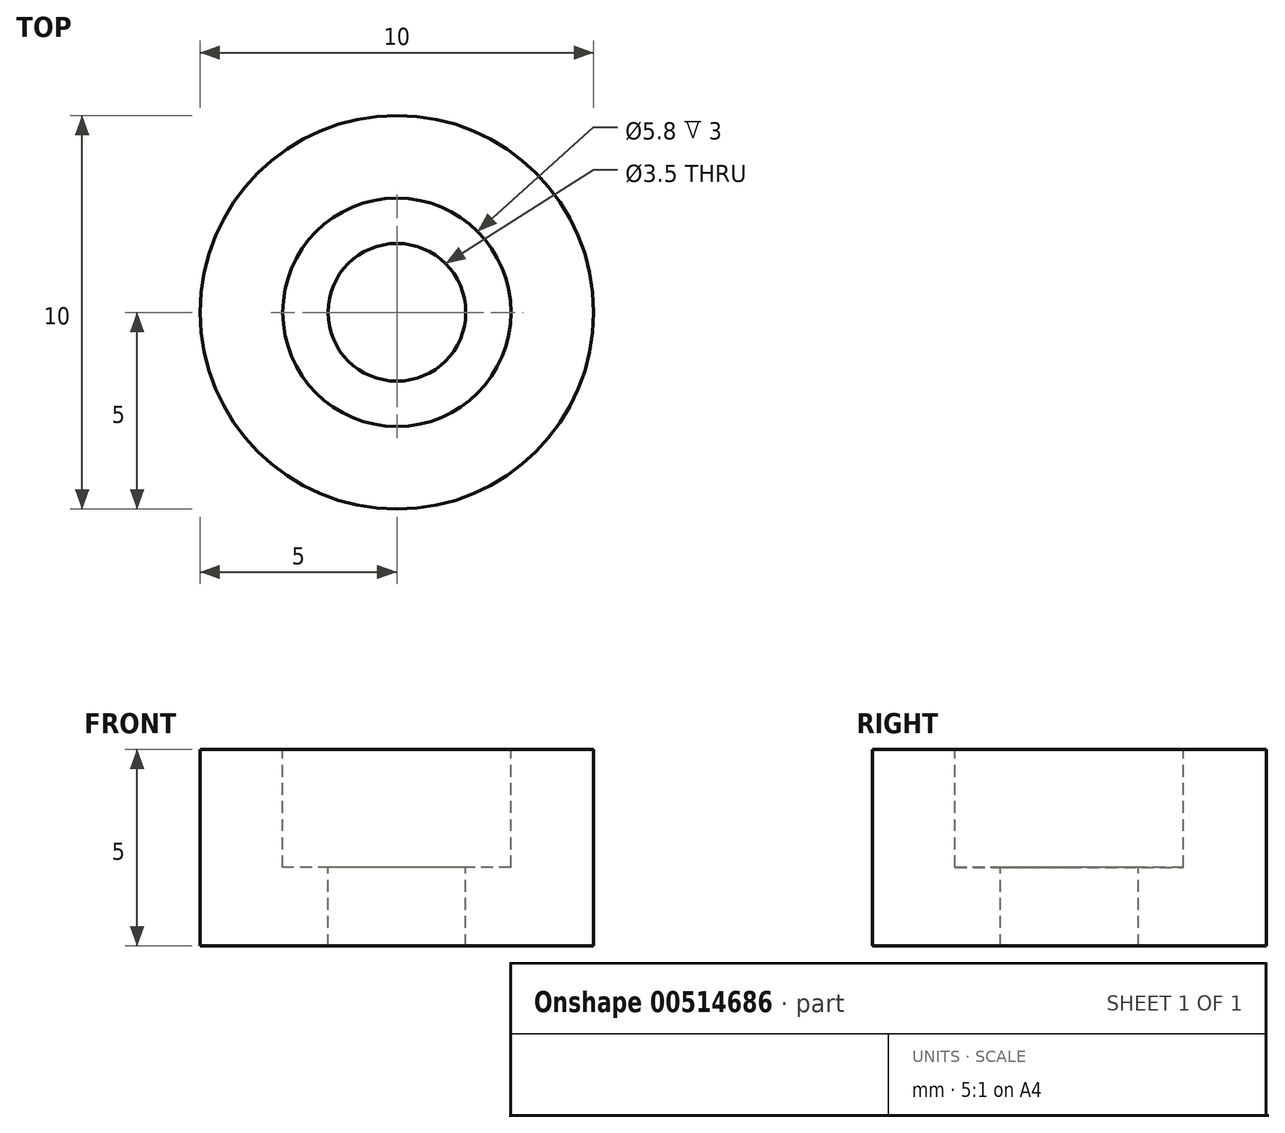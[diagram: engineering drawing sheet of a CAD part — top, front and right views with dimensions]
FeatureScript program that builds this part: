
annotation { "Feature Type Name" : "Feature", "Feature Type Description" : "" }
export const myFeature = defineFeature(function(context is Context, id is Id, definition is map)
    precondition{}
    {
        {
            var Q0;
            Q0=qCreatedBy(makeId("Top.planeOp"),FACE);
            var sketch = newSketch(context, id + "F0", { "sketchPlane" : qUnion([Q0])});
            skCircle(sketch, "E0", {"center": v(0, 0) * mm, "radius": 5 * mm});
            skSolve(sketch);
        }
        {
            var Q0;
            Q0=makeQuery(id+"F0.imprint","IMPRINT",FACE,{"disambiguationData":[TD([[makeQuery(id+"F0.imprint","IMPRINT",EDGE,{"derivedFrom":sQuery(id+"F0.wireOp",EDGE,"E0")}),1.0]])]});
            extrude(context, id + "F1", {"entities" : qUnion([Q0]), "depth" : 5 * mm, "offsetDistance" : 25 * mm});
        }
        {
            var Q0;
            Q0=makeQuery(id+"F1.opExtrude","CAP_FACE",FACE,{"disambiguationData":[OSD([sQuery(id+"F0.wireOp",EDGE,"E0")])],"isStart":false});
            var sketch = newSketch(context, id + "F2", { "sketchPlane" : qUnion([Q0])});
            skCircle(sketch, "E1", {"center": v(0, 0) * mm, "radius": 2.9 * mm});
            skSolve(sketch);
        }
        {
            var Q0;
            Q0=makeQuery(id+"F2.imprint","IMPRINT",FACE,{"disambiguationData":[TD([[makeQuery(id+"F2.imprint","IMPRINT",EDGE,{"derivedFrom":sQuery(id+"F2.wireOp",EDGE,"E1")}),1.0]])]});
            extrude(context, id + "F3", {"entities" : qUnion([Q0]), "operationType" : NewBodyOperationType.REMOVE, "oppositeDirection" : true, "depth" : 3 * mm, "offsetDistance" : 25 * mm});
        }
        {
            var Q0;
            Q0=makeQuery(id+"F3.boolean.opBoolean","COPY",FACE,{"derivedFrom":makeQuery(id+"F3.opExtrude","CAP_FACE",FACE,{"disambiguationData":[OSD([sQuery(id+"F2.wireOp",EDGE,"E1")])],"isStart":false})});
            var sketch = newSketch(context, id + "F4", { "sketchPlane" : qUnion([Q0])});
            skCircle(sketch, "E2", {"center": v(0, 0) * mm, "radius": 1.75 * mm});
            skSolve(sketch);
        }
        {
            var Q0;
            Q0=makeQuery(id+"F4.imprint","IMPRINT",FACE,{"disambiguationData":[TD([[makeQuery(id+"F4.imprint","IMPRINT",EDGE,{"derivedFrom":sQuery(id+"F4.wireOp",EDGE,"E2")}),1.0]])]});
            extrude(context, id + "F5", {"entities" : qUnion([Q0]), "operationType" : NewBodyOperationType.REMOVE, "endBound" : BoundingType.THROUGH_ALL, "oppositeDirection" : true, "depth" : 25 * mm, "offsetDistance" : 25 * mm});
        }
    });
